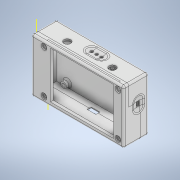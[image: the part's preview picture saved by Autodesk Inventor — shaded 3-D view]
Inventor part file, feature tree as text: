
AUTODESK INVENTOR PART (.ipt)
format: ipt  version: 2021.1 (Build 251245000, 245)  size: 1,057,280 bytes
history: native  units: mm
features: sketch x6, other x3, hole x2, fillet x2, split x1, emboss x1
ambient origin geometry x8: Origin, YZ Plane, XZ Plane, XY Plane, X Axis, Y Axis, Z Axis, Center Point
bodies: Solid1 (feature_tree), Solid2 (feature_tree), Solid3 (feature_tree)
feature tree (15):
  other  "original_body.ipt"
  hole  "Hole1"  [1 undecoded]
  hole  "Hole2"  [1 undecoded]
  fillet  "Fillet1"  [1 undecoded]
  fillet  "Fillet2"  [1 undecoded]
  sketch  "Sketch3"  dims[d8=3.3mm d9=6.0mm d10=6.0mm d11=1.25mm d12=90.0deg d13=8.0mm d14=0.0mm d15=1.5mm]
  sketch  "Sketch4"  dims[d16=1.5mm d17=0.3mm d18=0.0mm]
  sketch  "Sketch5"
  split  "Split1"
  emboss  "Emboss1"
  other  "Solid1::original_body.ipt"
  other  "TaggingFeature1"
  sketch  "Sketch1"  dims[d0=10.0mm]
  sketch  "Sketch2"  dims[d1=3.3mm d2=6.0mm d3=6.0mm d4=1.25mm d5=90.0deg d6=8.0mm d7=0.0mm]
  sketch  "Sketch6"
note: 4 required parameter values undecoded (feature->parameter linkage not recoverable at this tier; creation-order binding heuristic only, values carry confidence <= 0.55)
